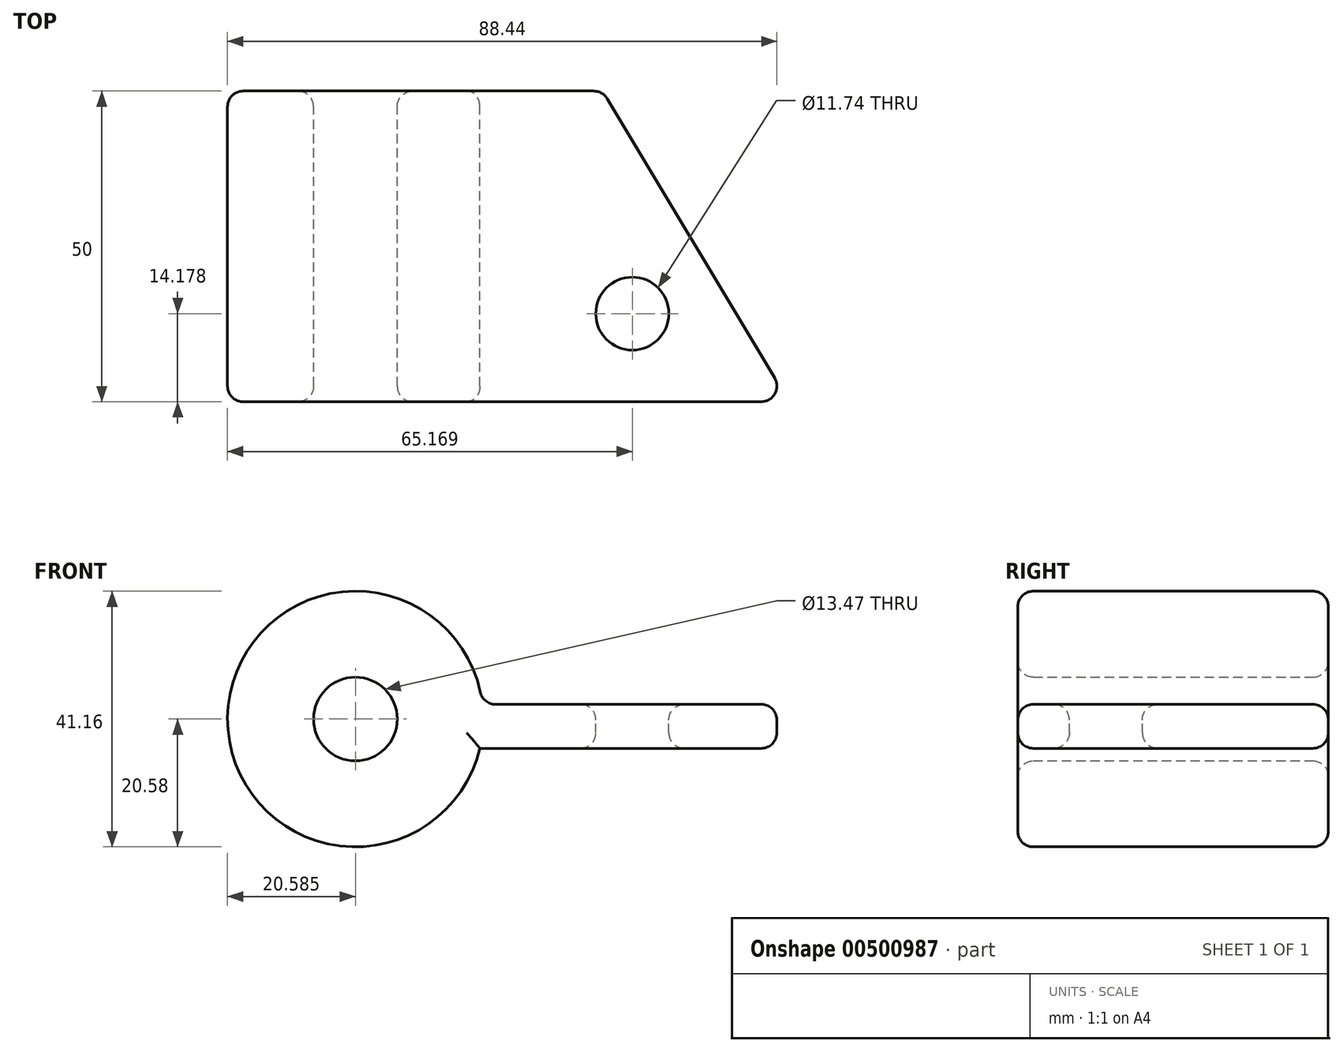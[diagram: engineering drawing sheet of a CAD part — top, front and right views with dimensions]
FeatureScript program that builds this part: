
annotation { "Feature Type Name" : "Feature", "Feature Type Description" : "" }
export const myFeature = defineFeature(function(context is Context, id is Id, definition is map)
    precondition{}
    {
        {
            var Q0;
            Q0=qCreatedBy(makeId("Front.planeOp"),FACE);
            var sketch = newSketch(context, id + "F0", { "sketchPlane" : qUnion([Q0])});
            skCircle(sketch, "E0", {"center": v(-44.76, 6.82) * mm, "radius": 20.58 * mm});
            skCircle(sketch, "E1", {"center": v(-44.76, 6.82) * mm, "radius": 6.74 * mm});
            skSolve(sketch);
        }
        {
            var Q0;
            Q0=makeQuery(id+"F0.imprint","IMPRINT",FACE,{"disambiguationData":[TD([[makeQuery(id+"F0.imprint","IMPRINT",EDGE,{"derivedFrom":sQuery(id+"F0.wireOp",EDGE,"E0")}),1.0]])]});
            extrude(context, id + "F1", {"entities" : qUnion([Q0]), "depth" : 50 * mm});
        }
        {
            var Q0;
            Q0=qCreatedBy(makeId("Right.planeOp"),FACE);
            var sketch = newSketch(context, id + "F2", { "sketchPlane" : qUnion([Q0])});
            skLineSegment(sketch, "E2.bottom", {"start": v(-50.14, 9.18) * mm, "end": v(0, 9.18) * mm});
            skLineSegment(sketch, "E2.top", {"start": v(-50.14, 2.1) * mm, "end": v(0, 2.1) * mm});
            skLineSegment(sketch, "E2.left", {"start": v(-50.14, 9.18) * mm, "end": v(-50.14, 2.1) * mm});
            skLineSegment(sketch, "E2.right", {"start": v(0, 9.18) * mm, "end": v(0, 2.1) * mm});
            skSolve(sketch);
        }
        {
            var Q0;
            Q0=makeQuery(id+"F2.imprint","IMPRINT",FACE,{"disambiguationData":[TD([[makeQuery(id+"F2.imprint","IMPRINT",EDGE,{"derivedFrom":sQuery(id+"F2.wireOp",EDGE,"E2.bottom")}),-1.0]])]});
            extrude(context, id + "F3", {"entities" : qUnion([Q0]), "oppositeDirection" : true, "depth" : 25 * mm});
        }
        {
            var Q0;
            Q0=makeQuery(id+"F3.opExtrude","SWEPT_BODY",BODY,{"disambiguationData":[OSD([sQuery(id+"F2.wireOp",EDGE,"E2.bottom"),sQuery(id+"F2.wireOp",EDGE,"E2.top"),sQuery(id+"F2.wireOp",EDGE,"E2.left"),sQuery(id+"F2.wireOp",EDGE,"E2.right")])]});
            var Q1;
            Q1=makeQuery(id+"F1.opExtrude","SWEPT_BODY",BODY,{"disambiguationData":[OSD([sQuery(id+"F0.wireOp",EDGE,"E0"),sQuery(id+"F0.wireOp",EDGE,"E1")])]});
            booleanBodies(context, id + "F4", {"operationType" : BooleanOperationType.UNION, "tools" : qUnion([Q0, Q1])});
        }
        {
            var Q0;
            Q0=makeQuery(id+"F3.opExtrude","CAP_FACE",FACE,{"disambiguationData":[OSD([sQuery(id+"F2.wireOp",EDGE,"E2.bottom"),sQuery(id+"F2.wireOp",EDGE,"E2.top"),sQuery(id+"F2.wireOp",EDGE,"E2.left"),sQuery(id+"F2.wireOp",EDGE,"E2.right")])],"isStart":true});
            extrude(context, id + "F5", {"entities" : qUnion([Q0]), "operationType" : NewBodyOperationType.ADD, "depth" : 25 * mm});
        }
        {
            var Q0;
            {var subQ0=sQuery(id+"F2.wireOp",EDGE,"E2.left");Q0=makeQuery(id+"F5.boolean.opBoolean","MERGE",FACE,{"derivedFrom":[makeQuery(id+"F3.opExtrude","SWEPT_FACE",FACE,{"disambiguationData":[OSD([subQ0])]}),makeQuery(id+"F5.opExtrude","SWEPT_FACE",FACE,{"disambiguationData":[OSD([subQ0])]})]});}
            var Q1;
            Q1=makeQuery(id+"F1.opExtrude","CAP_FACE",FACE,{"disambiguationData":[OSD([sQuery(id+"F0.wireOp",EDGE,"E0"),sQuery(id+"F0.wireOp",EDGE,"E1")])],"isStart":false});
            extrude(context, id + "F6", {"entities" : qUnion([Q0]), "operationType" : NewBodyOperationType.REMOVE, "endBound" : BoundingType.UP_TO_SURFACE, "oppositeDirection" : true, "endBoundEntityFace" : qUnion([Q1]), "depth" : 25 * mm});
        }
        {
            var Q0;
            {var subQ0=sQuery(id+"F2.wireOp",EDGE,"E2.bottom");Q0=makeQuery(id+"F5.boolean.opBoolean","MERGE",FACE,{"derivedFrom":[makeQuery(id+"F3.opExtrude","SWEPT_FACE",FACE,{"disambiguationData":[OSD([subQ0])]}),makeQuery(id+"F5.opExtrude","SWEPT_FACE",FACE,{"disambiguationData":[OSD([subQ0])]})]});}
            var sketch = newSketch(context, id + "F7", { "sketchPlane" : qUnion([Q0])});
            skLineSegment(sketch, "E3", {"start": v(25, -50) * mm, "end": v(-4.96, 0) * mm});
            skSolve(sketch);
        }
        {
            var Q0;
            {var subQ3=sQuery(id+"F7.wireOp",EDGE,"E3");Q0=makeQuery(id+"F7.imprint","IMPRINT",FACE,{"disambiguationData":[TD([[makeQuery(id+"F7.imprint","IMPRINT",EDGE,{"derivedFrom":subQ3}),-1.0]])]});}
            extrude(context, id + "F8", {"entities" : qUnion([Q0]), "operationType" : NewBodyOperationType.REMOVE, "endBound" : BoundingType.THROUGH_ALL, "oppositeDirection" : true, "depth" : 25 * mm});
        }
        {
            var Q0;
            {var subQ0=sQuery(id+"F2.wireOp",EDGE,"E2.bottom");Q0=makeQuery(id+"F5.boolean.opBoolean","MERGE",FACE,{"derivedFrom":[makeQuery(id+"F3.opExtrude","SWEPT_FACE",FACE,{"disambiguationData":[OSD([subQ0])]}),makeQuery(id+"F5.opExtrude","SWEPT_FACE",FACE,{"disambiguationData":[OSD([subQ0])]})]});}
            var sketch = newSketch(context, id + "F9", { "sketchPlane" : qUnion([Q0])});
            skCircle(sketch, "E4", {"center": v(-0.18, -35.82) * mm, "radius": 5.87 * mm});
            skSolve(sketch);
        }
        {
            var Q0;
            Q0=makeQuery(id+"F9.imprint","IMPRINT",FACE,{"disambiguationData":[TD([[makeQuery(id+"F9.imprint","IMPRINT",EDGE,{"derivedFrom":sQuery(id+"F9.wireOp",EDGE,"E4")}),1.0]])]});
            extrude(context, id + "F10", {"entities" : qUnion([Q0]), "operationType" : NewBodyOperationType.REMOVE, "endBound" : BoundingType.THROUGH_ALL, "oppositeDirection" : true, "depth" : 25 * mm});
        }
        {
            var Q0;
            {var subQ0=sQuery(id+"F2.wireOp",EDGE,"E2.bottom");Q0=makeQuery(id+"F5.boolean.opBoolean","MERGE",FACE,{"derivedFrom":[makeQuery(id+"F3.opExtrude","SWEPT_FACE",FACE,{"disambiguationData":[OSD([subQ0])]}),makeQuery(id+"F5.opExtrude","SWEPT_FACE",FACE,{"disambiguationData":[OSD([subQ0])]})]});}
            var Q1;
            Q1=makeQuery(id+"F1.opExtrude","SWEPT_FACE",FACE,{"disambiguationData":[OSD([sQuery(id+"F0.wireOp",EDGE,"E1")])]});
            var Q2;
            Q2=makeQuery(id+"F10.boolean.opBoolean","COPY",FACE,{"derivedFrom":makeQuery(id+"F10.opExtrude","SWEPT_FACE",FACE,{"disambiguationData":[OSD([sQuery(id+"F9.wireOp",EDGE,"E4")])]})});
            var Q3;
            {var subQ0=sQuery(id+"F0.wireOp",EDGE,"E1");var subQ1=sQuery(id+"F0.wireOp",EDGE,"E0");Q3=makeQuery(id+"F6.boolean.opBoolean","MERGE",FACE,{"derivedFrom":[makeQuery(id+"F1.opExtrude","CAP_FACE",FACE,{"disambiguationData":[OSD([subQ1,subQ0])],"isStart":false}),makeQuery(id+"F6.opExtrude","CAP_FACE",FACE,{"disambiguationData":[OSD([subQ1,subQ0])],"isStart":false})]});}
            var Q4;
            {var subQ0=sQuery(id+"F2.wireOp",EDGE,"E2.right");Q4=makeQuery(id+"F5.boolean.opBoolean","MERGE",FACE,{"derivedFrom":[makeQuery(id+"F4.opBoolean","MERGE",FACE,{"derivedFrom":[makeQuery(id+"F1.opExtrude","CAP_FACE",FACE,{"disambiguationData":[OSD([sQuery(id+"F0.wireOp",EDGE,"E0"),sQuery(id+"F0.wireOp",EDGE,"E1")])],"isStart":true}),makeQuery(id+"F3.opExtrude","SWEPT_FACE",FACE,{"disambiguationData":[OSD([subQ0])]})]}),makeQuery(id+"F5.opExtrude","SWEPT_FACE",FACE,{"disambiguationData":[OSD([subQ0])]})]});}
            var Q5;
            Q5=makeQuery(id+"F8.boolean.opBoolean","COPY",FACE,{"derivedFrom":makeQuery(id+"F8.opExtrude","SWEPT_FACE",FACE,{"disambiguationData":[OSD([sQuery(id+"F7.wireOp",EDGE,"E3")])]})});
            fillet(context, id + "F11", {"entities" : qUnion([Q0, Q1, Q2, Q3, Q4, Q5]), "radius" : 2.5 * mm, "tangentPropagation" : true, "allowEdgeOverflow" : false});
        }
    });
